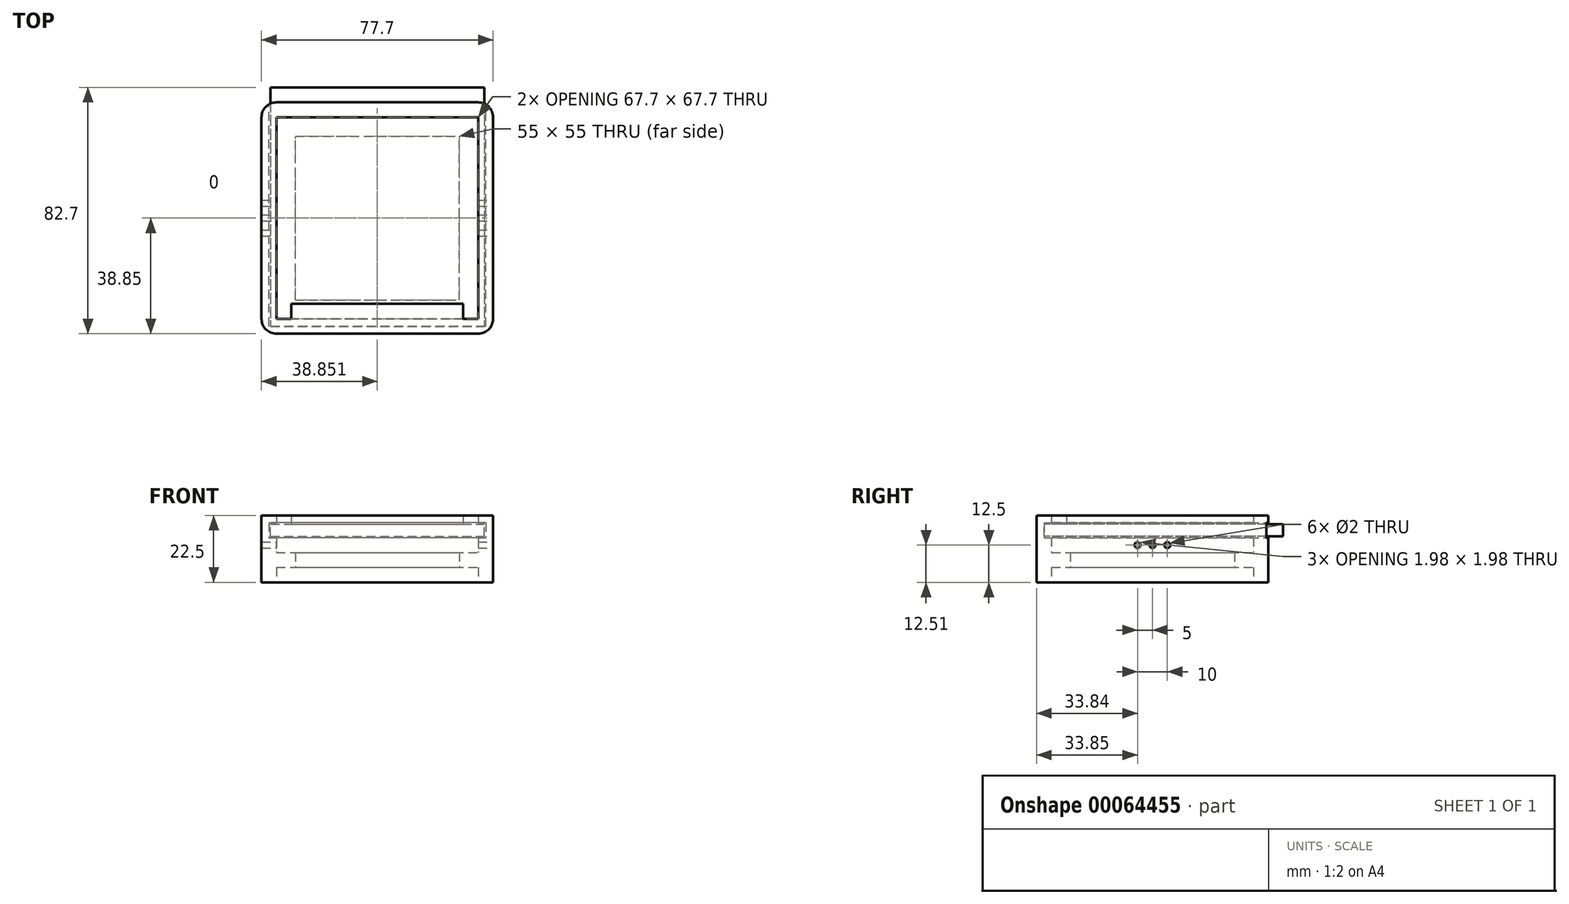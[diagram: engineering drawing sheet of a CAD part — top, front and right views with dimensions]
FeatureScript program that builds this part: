
annotation { "Feature Type Name" : "Feature", "Feature Type Description" : "" }
export const myFeature = defineFeature(function(context is Context, id is Id, definition is map)
    precondition{}
    {
        {
            var Q0;
            Q0=qCreatedBy(makeId("Top.planeOp"),FACE);
            var sketch = newSketch(context, id + "F0", { "sketchPlane" : qUnion([Q0])});
            skLineSegment(sketch, "E0.bottom", {"start": v(0.4, 0) * mm, "end": v(68.1, 0) * mm});
            skLineSegment(sketch, "E0.top", {"start": v(0.4, 67.7) * mm, "end": v(68.1, 67.7) * mm});
            skLineSegment(sketch, "E0.left", {"start": v(0.4, 0) * mm, "end": v(0.4, 67.7) * mm});
            skLineSegment(sketch, "E0.right", {"start": v(68.1, 0) * mm, "end": v(68.1, 67.7) * mm});
            skLineSegment(sketch, "E1.0", {"start": v(0.4, 72.7) * mm, "end": v(68.1, 72.7) * mm});
            skLineSegment(sketch, "E1.1", {"start": v(-4.6, 0) * mm, "end": v(-4.6, 67.7) * mm});
            skLineSegment(sketch, "E1.2", {"start": v(0.4, -5) * mm, "end": v(68.1, -5) * mm});
            skLineSegment(sketch, "E1.3", {"start": v(73.1, 0) * mm, "end": v(73.1, 67.7) * mm});
            skPoint(sketch, "E2.visualSharp", {"position": v(-4.6, 72.7) * mm});
            skArc(sketch, "E2.filletArc", {"start": v(0.4, 72.7) * mm, "mid": v(-3.13, 71.24) * mm, "end": v(-4.6, 67.7) * mm});
            skPoint(sketch, "E3.visualSharp", {"position": v(73.1, 72.7) * mm});
            skArc(sketch, "E3.filletArc", {"start": v(73.1, 67.7) * mm, "mid": v(71.64, 71.24) * mm, "end": v(68.1, 72.7) * mm});
            skPoint(sketch, "E4.visualSharp", {"position": v(73.1, -5) * mm});
            skArc(sketch, "E4.filletArc", {"start": v(68.1, -5) * mm, "mid": v(71.64, -3.54) * mm, "end": v(73.1, 0) * mm});
            skPoint(sketch, "E5.visualSharp", {"position": v(-4.6, -5) * mm});
            skArc(sketch, "E5.filletArc", {"start": v(-4.6, 0) * mm, "mid": v(-3.13, -3.54) * mm, "end": v(0.4, -5) * mm});
            skSolve(sketch);
        }
        {
            var Q0;
            Q0=makeQuery(id+"F0.imprint","IMPRINT",FACE,{"disambiguationData":[TD([[makeQuery(id+"F0.imprint","IMPRINT",EDGE,{"derivedFrom":sQuery(id+"F0.wireOp",EDGE,"E0.bottom")}),-1.0]])]});
            extrude(context, id + "F1", {"entities" : qUnion([Q0]), "depth" : 22.5 * mm});
        }
        {
            var Q0;
            Q0=qCreatedBy(makeId("Top.planeOp"),FACE);
            var sketch = newSketch(context, id + "F2", { "sketchPlane" : qUnion([Q0])});
            skLineSegment(sketch, "E6.bottom", {"start": v(0.4, 0) * mm, "end": v(68.1, 0) * mm});
            skLineSegment(sketch, "E6.top", {"start": v(0.4, 67.7) * mm, "end": v(68.1, 67.7) * mm});
            skLineSegment(sketch, "E6.left", {"start": v(0.4, 0) * mm, "end": v(0.4, 67.7) * mm});
            skLineSegment(sketch, "E6.right", {"start": v(68.1, 0) * mm, "end": v(68.1, 67.7) * mm});
            skLineSegment(sketch, "E7.0", {"start": v(6.75, 6.35) * mm, "end": v(61.75, 6.35) * mm});
            skLineSegment(sketch, "E7.1", {"start": v(6.75, 6.35) * mm, "end": v(6.75, 61.35) * mm});
            skLineSegment(sketch, "E7.2", {"start": v(6.75, 61.35) * mm, "end": v(61.75, 61.35) * mm});
            skLineSegment(sketch, "E7.3", {"start": v(61.75, 6.35) * mm, "end": v(61.75, 61.35) * mm});
            skSolve(sketch);
        }
        {
            var Q0;
            Q0=makeQuery(id+"F2.imprint","IMPRINT",FACE,{"disambiguationData":[TD([[makeQuery(id+"F2.imprint","IMPRINT",EDGE,{"derivedFrom":sQuery(id+"F2.wireOp",EDGE,"E6.bottom")}),1.0]])]});
            extrude(context, id + "F3", {"entities" : qUnion([Q0]), "operationType" : NewBodyOperationType.ADD, "depth" : 10 * mm, "hasSecondDirection" : true, "secondDirectionOppositeDirection" : false, "secondDirectionDepth" : 5 * mm});
        }
        {
            var Q0;
            Q0=makeQuery(id+"F3.boolean.opBoolean","MERGE",FACE,{"derivedFrom":[makeQuery(id+"F1.opExtrude","CAP_FACE",FACE,{"disambiguationData":[OSD([sQuery(id+"F0.wireOp",EDGE,"E0.bottom"),sQuery(id+"F0.wireOp",EDGE,"E0.top"),sQuery(id+"F0.wireOp",EDGE,"E0.left"),sQuery(id+"F0.wireOp",EDGE,"E0.right"),sQuery(id+"F0.wireOp",EDGE,"E1.0"),sQuery(id+"F0.wireOp",EDGE,"E1.1"),sQuery(id+"F0.wireOp",EDGE,"E1.2"),sQuery(id+"F0.wireOp",EDGE,"E1.3"),sQuery(id+"F0.wireOp",EDGE,"E2.filletArc"),sQuery(id+"F0.wireOp",EDGE,"E3.filletArc"),sQuery(id+"F0.wireOp",EDGE,"E4.filletArc"),sQuery(id+"F0.wireOp",EDGE,"E5.filletArc")])],"isStart":false}),makeQuery(id+"F3.opExtrude","CAP_FACE",FACE,{"disambiguationData":[OSD([sQuery(id+"F2.wireOp",EDGE,"E6.bottom"),sQuery(id+"F2.wireOp",EDGE,"E6.top"),sQuery(id+"F2.wireOp",EDGE,"E6.left"),sQuery(id+"F2.wireOp",EDGE,"E6.right"),sQuery(id+"F2.wireOp",EDGE,"E7.0"),sQuery(id+"F2.wireOp",EDGE,"E7.1"),sQuery(id+"F2.wireOp",EDGE,"E7.2"),sQuery(id+"F2.wireOp",EDGE,"E7.3")])],"isStart":true})]});
            var sketch = newSketch(context, id + "F4", { "sketchPlane" : qUnion([Q0])});
            skSolve(sketch);
        }
        {
            var Q0;
            Q0=makeQuery(id+"F1.opExtrude","SWEPT_FACE",FACE,{"disambiguationData":[OSD([sQuery(id+"F0.wireOp",EDGE,"E1.3")])]});
            var sketch = newSketch(context, id + "F5", { "sketchPlane" : qUnion([Q0])});
            skCircle(sketch, "E8", {"center": v(33.85, 12.5) * mm, "radius": 1 * mm});
            skCircle(sketch, "E9", {"center": v(38.85, 12.5) * mm, "radius": 1 * mm});
            skCircle(sketch, "E10", {"center": v(28.85, 12.5) * mm, "radius": 1 * mm});
            skLineSegment(sketch, "E11", {"start": v(0, 12.5) * mm, "end": v(67.7, 12.5) * mm});
            skSolve(sketch);
        }
        {
            var Q0;
            Q0 = qSketchRegion(id + "F5", true);
            extrude(context, id + "F6", {"entities" : qUnion([Q0]), "operationType" : NewBodyOperationType.REMOVE, "oppositeDirection" : true, "depth" : 100 * mm});
        }
        {
            var Q0;
            Q0=makeQuery(id+"F1.opExtrude","SWEPT_FACE",FACE,{"disambiguationData":[OSD([sQuery(id+"F0.wireOp",EDGE,"E1.0")])]});
            var sketch = newSketch(context, id + "F7", { "sketchPlane" : qUnion([Q0])});
            skLineSegment(sketch, "E12.bottom", {"start": v(-70.6, 20) * mm, "end": v(2.1, 20) * mm});
            skLineSegment(sketch, "E12.top", {"start": v(-70.6, 15) * mm, "end": v(2.1, 15) * mm});
            skLineSegment(sketch, "E12.left", {"start": v(-70.6, 20) * mm, "end": v(-70.6, 15) * mm});
            skLineSegment(sketch, "E12.right", {"start": v(2.1, 20) * mm, "end": v(2.1, 15) * mm});
            skSolve(sketch);
        }
        {
            var Q0;
            Q0 = qSketchRegion(id + "F7", true);
            extrude(context, id + "F8", {"entities" : qUnion([Q0]), "operationType" : NewBodyOperationType.REMOVE, "oppositeDirection" : true, "depth" : 62.5 * mm + 12.7 * mm});
        }
        {
            var Q0;
            {var subQ2=sQuery(id+"F0.wireOp",EDGE,"E1.0");Q0=makeQuery(id+"F8.boolean.opBoolean","SPLIT",FACE,{"disambiguationData":[TD([makeQuery(id+"F8.opExtrude","SWEPT_FACE",FACE,{"disambiguationData":[OSD([sQuery(id+"F7.wireOp",EDGE,"E12.top")])]})])],"derivedFrom":makeQuery(id+"F1.opExtrude","SWEPT_FACE",FACE,{"disambiguationData":[OSD([subQ2])]})});}
            var sketch = newSketch(context, id + "F9", { "sketchPlane" : qUnion([Q0])});
            skLineSegment(sketch, "E13.0", {"start": v(-68.1, 15.5) * mm, "end": v(-70.1, 15.5) * mm});
            skLineSegment(sketch, "E13.1", {"start": v(-70.1, 15.5) * mm, "end": v(-70.1, 19.5) * mm});
            skLineSegment(sketch, "E13.2", {"start": v(-68.1, 15.5) * mm, "end": v(-0.4, 15.5) * mm});
            skLineSegment(sketch, "E13.3", {"start": v(-68.1, 19.5) * mm, "end": v(-70.1, 19.5) * mm});
            skLineSegment(sketch, "E13.4", {"start": v(1.6, 15.5) * mm, "end": v(-0.4, 15.5) * mm});
            skLineSegment(sketch, "E13.5", {"start": v(1.6, 15.5) * mm, "end": v(1.6, 19.5) * mm});
            skLineSegment(sketch, "E13.6", {"start": v(1.6, 19.5) * mm, "end": v(-0.4, 19.5) * mm});
            skLineSegment(sketch, "E13.7", {"start": v(-68.1, 19.5) * mm, "end": v(-0.4, 19.5) * mm});
            skSolve(sketch);
        }
        {
            var Q0;
            Q0 = qSketchRegion(id + "F9", true);
            extrude(context, id + "F10", {"entities" : qUnion([Q0]), "depth" : 5 * mm, "hasSecondDirection" : true, "secondDirectionOppositeDirection" : true, "secondDirectionDepth" : 62.5 * mm + 12.7 * mm});
        }
        {
            var Q0;
            Q0=makeQuery(id+"F10.opExtrude","SWEPT_FACE",FACE,{"disambiguationData":[OSD([sQuery(id+"F9.wireOp",EDGE,"E13.3"),sQuery(id+"F9.wireOp",EDGE,"E13.6"),sQuery(id+"F9.wireOp",EDGE,"E13.7")])]});
            var sketch = newSketch(context, id + "F11", { "sketchPlane" : qUnion([Q0])});
            skLineSegment(sketch, "E14.bottom", {"start": v(5.4, 5) * mm, "end": v(63.1, 5) * mm});
            skLineSegment(sketch, "E14.top", {"start": v(5.4, 0) * mm, "end": v(63.1, 0) * mm});
            skLineSegment(sketch, "E14.left", {"start": v(5.4, 5) * mm, "end": v(5.4, 0) * mm});
            skLineSegment(sketch, "E14.right", {"start": v(63.1, 5) * mm, "end": v(63.1, 0) * mm});
            skSolve(sketch);
        }
        {
            var Q0;
            Q0 = qSketchRegion(id + "F11", true);
            extrude(context, id + "F12", {"entities" : qUnion([Q0]), "operationType" : NewBodyOperationType.ADD, "depth" : 3 * mm});
        }
    });
